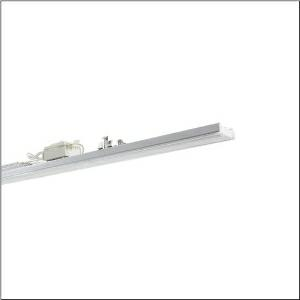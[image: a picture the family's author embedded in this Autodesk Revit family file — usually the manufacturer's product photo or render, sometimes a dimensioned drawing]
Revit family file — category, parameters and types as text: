
# Revit family: licross_r__21_recessed_mo_52tl18dv4e5g_229a
name_source: partatom
category: Lighting Fixtures
units: mm (PartAtom-declared; Revit-internal decimal feet)

## family parameters
Cut with Voids When Loaded = No
Host = Face
Light Source = No
Part Type = Normal
Room Calculation Point = No
Round Connector Dimension = Use Diameter
Shared = No

## types (1)
- --- (1 x LED, 14980 lm, 85.3 W, 4000K)
    Apparent Load = 85 VA
    CIE Flux Codes = 79 95 99 100 100
    Color Rendering = 80
    Color Temperature = 4000K
    Default Elevation = 1800 mm
    Description = Licross® 21 Recessed MO, luminaire insert, of sheet steel, galvanised, coil coated, white, length: 2.250mm, width: 66mm, height: 67mm, LED rated luminous flux: 14.980lm, light colour: 840, control gear: DALI 2, with plug, 5-pole, with phase selection, mains connection: 220..240V, AC, 50/60Hz, rated input power: 85W, halogen-free wiring, primary light control with lens, of plastic, primary optical cover: cover, of PMMA, light emission: direct distribution, primary light characteristic: symmetric, protection rating (complete): IP40, insulation class (complete): insulation class I (protective earthing), certification: CE, ENEC, VDE, UKCA, protection symbol: D if used in an environment without relevant dust loads with corresponding accessories, impact resistance: IK06, permissible ambient temperature for indoor applications: -25..+35°C, corresponds to IFS (International Featured Standards) requirements for safety and quality in the food industry, reducing of maximum allowable ambient temperature of 5°C with ceiling mounting, LABS conformity tested according to VDMA 24364:2018-05, packaging unit: 1 piece
    Height = 58 mm
    Lamp = 1 x LED
    Lamp Light Flux = 14980 lm
    Lamp Power = 85.3 W
    Lamp count = 1
    Length = 2250 mm
    Luminous efficacy = 176 lm/W
    Manufacturer = Siteco
    ModVariant = No
    Model = 52TL18DV4E5G
    Mounting Place = Ceiling
    Mounting Type = Pendant
    Number of Poles = 1
    OnlyDefault = Yes
    Power Factor = 1
    Product Name = Licross® 21 Recessed MO
    Product group = luminaire insert
    ProductGroupID = 902
    Protection Class = Protection class I
    Protection Degree = IP 40
    RLX_Detail_Level = 1
    RLX_Emergency_Light_Flux = 0 lm
    RLX_Emergency_Type = 0
    RLX_Emergency_Type_DB = No
    RlxData = <blob elided: 29593 chars, md5=9e4e66be>
    Socket = socket
    Standby Power = 0 W
    System Light Flux = 14980 lm
    System Power = 85 W
    Type Comments = factory setting: luminous flux: 100 % | dim-lin: 254 | 390 mA
    Type Image = l_1296930.jpg
    URL = http://relux.com
    VarID = @adj_126050
    Voltage = 0 V
    Weight = 0.00 kg
    Width = 66 mm

## geometry (parser evidence)
native form markers: Blend x4, Sweep x10
no freeform markers — native parametric forms only
